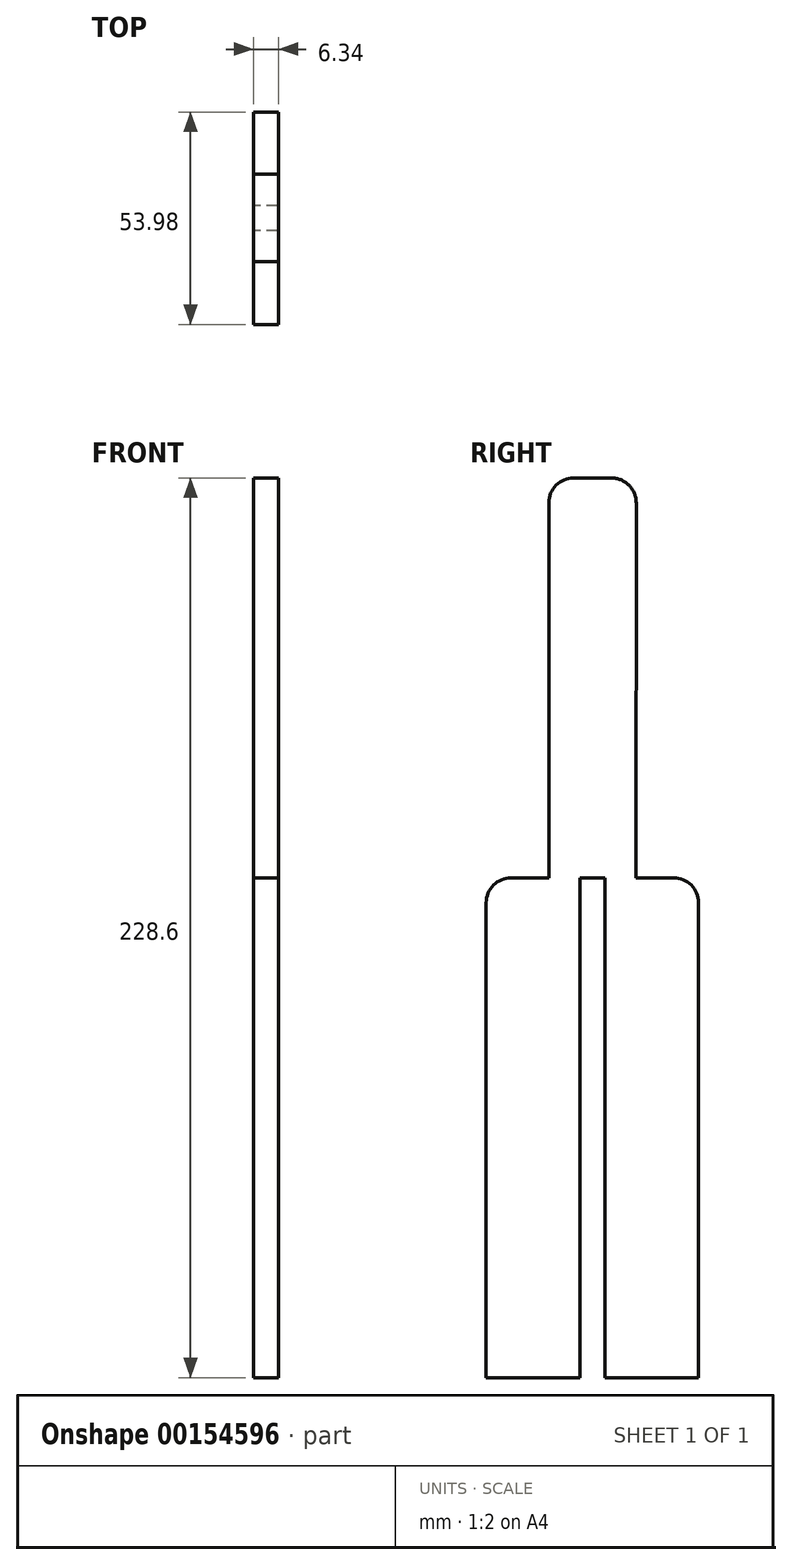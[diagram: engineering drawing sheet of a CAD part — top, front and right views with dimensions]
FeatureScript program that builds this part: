
annotation { "Feature Type Name" : "Feature", "Feature Type Description" : "" }
export const myFeature = defineFeature(function(context is Context, id is Id, definition is map)
    precondition{}
    {
        {
            var Q0;
            Q0=qCreatedBy(makeId("Right.planeOp"),FACE);
            var sketch = newSketch(context, id + "F0", { "sketchPlane" : qUnion([Q0])});
            skLineSegment(sketch, "E0.bottom", {"start": v(26.99, -63.5) * mm, "end": v(3.18, -63.5) * mm});
            skLineSegment(sketch, "E0.top", {"start": v(20.64, 63.5) * mm, "end": v(17.46, 63.5) * mm});
            skLineSegment(sketch, "E0.left", {"start": v(26.99, -63.5) * mm, "end": v(26.99, 57.15) * mm});
            skLineSegment(sketch, "E0.right", {"start": v(-26.99, -63.5) * mm, "end": v(-26.99, 57.15) * mm});
            skPoint(sketch, "E0.middle", {"position": v(0, 0) * mm});
            skLineSegment(sketch, "E1", {"start": v(-11.1, 63.5) * mm, "end": v(-11.1, 158.75) * mm});
            skLineSegment(sketch, "E2", {"start": v(-4.75, 165.1) * mm, "end": v(4.77, 165.1) * mm});
            skLineSegment(sketch, "E3", {"start": v(11.12, 158.75) * mm, "end": v(11.11, 63.5) * mm});
            skLineSegment(sketch, "E4.trimOffspring", {"start": v(-17.45, 63.5) * mm, "end": v(-20.64, 63.5) * mm});
            skPoint(sketch, "E5.start.orphan", {"position": v(0, -63.5) * mm});
            skPoint(sketch, "E6.visualSharp", {"position": v(-11.1, 63.5) * mm});
            skPoint(sketch, "E7.visualSharp", {"position": v(11.11, 63.5) * mm});
            skPoint(sketch, "E8.visualSharp", {"position": v(-26.99, 63.5) * mm});
            skArc(sketch, "E8.filletArc", {"start": v(-20.64, 63.5) * mm, "mid": v(-25.13, 61.64) * mm, "end": v(-26.99, 57.15) * mm});
            skPoint(sketch, "E9.visualSharp", {"position": v(26.99, 63.5) * mm});
            skArc(sketch, "E9.filletArc", {"start": v(26.99, 57.15) * mm, "mid": v(25.13, 61.64) * mm, "end": v(20.64, 63.5) * mm});
            skPoint(sketch, "E10.visualSharp", {"position": v(11.13, 165.1) * mm});
            skArc(sketch, "E10.filletArc", {"start": v(11.12, 158.75) * mm, "mid": v(9.26, 163.24) * mm, "end": v(4.77, 165.1) * mm});
            skPoint(sketch, "E11.visualSharp", {"position": v(-11.1, 165.1) * mm});
            skArc(sketch, "E11.filletArc", {"start": v(-4.75, 165.1) * mm, "mid": v(-9.24, 163.24) * mm, "end": v(-11.1, 158.75) * mm});
            skLineSegment(sketch, "E12", {"start": v(-3.18, -63.5) * mm, "end": v(-3.18, 63.5) * mm});
            skLineSegment(sketch, "E13", {"start": v(-3.18, 63.5) * mm, "end": v(3.17, 63.5) * mm});
            skLineSegment(sketch, "E14", {"start": v(3.17, 63.5) * mm, "end": v(3.17, -63.5) * mm});
            skLineSegment(sketch, "E15.trimOffspring", {"start": v(-3.18, -63.5) * mm, "end": v(-26.99, -63.5) * mm});
            skLineSegment(sketch, "E16", {"start": v(-17.45, 63.5) * mm, "end": v(-11.1, 63.5) * mm});
            skLineSegment(sketch, "E17", {"start": v(11.11, 63.5) * mm, "end": v(17.46, 63.5) * mm});
            skSolve(sketch);
        }
        {
            var Q0;
            Q0=qSketchRegion(id+"F0",true);
            extrude(context, id + "F1", {"entities" : qUnion([Q0]), "endBound" : BoundingType.SYMMETRIC, "depth" : 6.35 * mm});
        }
    });
